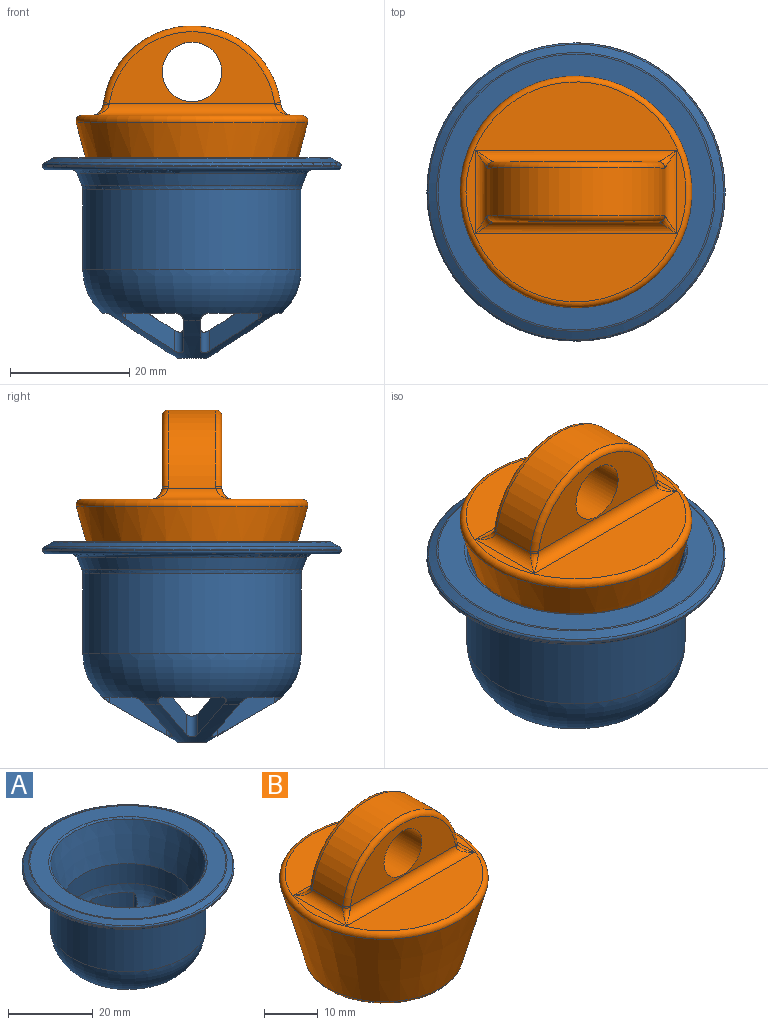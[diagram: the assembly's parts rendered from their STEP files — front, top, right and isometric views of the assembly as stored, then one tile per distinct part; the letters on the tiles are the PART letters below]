
ASSEMBLY  parts=2 mates=1
PART A: 55 faces, bbox 55.1x55.1x34.5 mm
  f0: torus R=8.3mm, axis (0,0,-1), area 945.5mm2, adj f1,f9,f14,f15,f16,f17,f18,f20
  f1: cone r=0mm half-angle=60deg, axis (0,0,1), area 270.6mm2, adj f0,f13,f14,f15,f19,f20,f21,f25
  f2: cone r=0mm half-angle=60deg, axis (0,0,1), area 183.2mm2, adj f3,f13,f14,f15,f19,f20,f21,f25
  f3: torus R=5.3mm, axis (0,0,-1), area 393.2mm2, adj f2,f10,f14,f15,f16,f17,f18,f20
  f4: cone r=25mm half-angle=60deg, axis (0,0,-1), area 238.5mm2, adj f50,f53
  f5: cylinder r=25mm len=50mm, axis (0,0,-1), area 33.2mm2, adj f50,f51
  f6: plane 49x49mm, normal (0,0,-1), area 606.8mm2, adj f7,f51
  f7: torus R=20.18mm, axis (0,0,-1), area 147mm2, adj f6,f8
  f8: cone r=18.3mm half-angle=21.8deg, axis (0,0,1), area 256.8mm2, adj f7,f54
  f9: cylinder r=18.3mm len=36.6mm, axis (0,0,-1), area 1526.5mm2, adj f0,f54
  f10: cylinder r=15.3mm len=30.6mm, axis (0,0,-1), area 551.1mm2, adj f3,f11
  f11: cone r=18.3mm half-angle=15deg, axis (0,0,1), area 1179.5mm2, adj f10,f52
  f12: plane 46.27x46.27mm, normal (0,0,1), area 584.7mm2, adj f52,f53
  f13: cylinder r=1mm len=3.46mm, axis (0,0,1), area 7.3mm2, adj f1,f2,f14,f15
  f14: plane 11.22x9.15mm, normal (-0.5,0.87,0), area 34.2mm2, adj f0,f1,f2,f3,f13,f18
  f15: plane 11.22x9.15mm, normal (-0.5,-0.87,0), area 34.2mm2, adj f0,f1,f2,f3,f13,f16
  f16: cylinder r=1mm len=7.62mm, axis (0,0,1), area 10.1mm2, adj f0,f3,f15,f17
  f17: cylinder r=15mm len=10.12mm, axis (0,0,1), area 69.4mm2, adj f0,f3,f16,f18
  f18: cylinder r=1mm len=7.62mm, axis (0,0,1), area 10.1mm2, adj f0,f3,f14,f17
  f19: cylinder r=1mm len=3.46mm, axis (0,0,1), area 7.3mm2, adj f1,f2,f20,f21
  f20: plane 11.22x9.15mm, normal (0.5,0.87,0), area 34.2mm2, adj f0,f1,f2,f3,f19,f24
  f21: plane 11.22x10.41mm, normal (-1,0,0), area 34.2mm2, adj f0,f1,f2,f3,f19,f22
  f22: cylinder r=1mm len=7.62mm, axis (0,0,1), area 10.1mm2, adj f0,f3,f21,f23
  f23: cylinder r=15mm len=8.76mm, axis (0,0,1), area 69.4mm2, adj f0,f3,f22,f24
  f24: cylinder r=1mm len=7.62mm, axis (0,0,1), area 10.1mm2, adj f0,f3,f20,f23
  f25: cylinder r=1mm len=3.46mm, axis (0,0,1), area 7.3mm2, adj f1,f2,f26,f27
  f26: plane 11.22x10.41mm, normal (-1,0,0), area 34.2mm2, adj f0,f1,f2,f3,f25,f30
  f27: plane 11.22x9.15mm, normal (0.5,-0.87,0), area 34.2mm2, adj f0,f1,f2,f3,f25,f28
  f28: cylinder r=1mm len=7.62mm, axis (0,0,1), area 10.1mm2, adj f0,f3,f27,f29
  f29: cylinder r=15mm len=8.76mm, axis (0,0,1), area 69.4mm2, adj f0,f3,f28,f30
  f30: cylinder r=1mm len=7.62mm, axis (0,0,1), area 10.1mm2, adj f0,f3,f26,f29
  f31: cylinder r=1mm len=3.46mm, axis (0,0,1), area 7.3mm2, adj f1,f2,f32,f33
  f32: plane 11.22x9.15mm, normal (-0.5,-0.87,0), area 34.2mm2, adj f0,f1,f2,f3,f31,f36
  f33: plane 11.22x10.41mm, normal (1,0,0), area 34.2mm2, adj f0,f1,f2,f3,f31,f34
  f34: cylinder r=1mm len=7.62mm, axis (0,0,1), area 10.1mm2, adj f0,f3,f33,f35
  f35: cylinder r=15mm len=8.76mm, axis (0,0,1), area 69.4mm2, adj f0,f3,f34,f36
  f36: cylinder r=1mm len=7.62mm, axis (0,0,1), area 10.1mm2, adj f0,f3,f32,f35
  f37: cylinder r=1mm len=3.46mm, axis (0,0,1), area 7.3mm2, adj f1,f2,f38,f39
  f38: plane 11.22x10.41mm, normal (1,0,0), area 34.2mm2, adj f0,f1,f2,f3,f37,f42
  f39: plane 11.22x9.15mm, normal (-0.5,0.87,0), area 34.2mm2, adj f0,f1,f2,f3,f37,f40
  f40: cylinder r=1mm len=7.62mm, axis (0,0,1), area 10.1mm2, adj f0,f3,f39,f41
  f41: cylinder r=15mm len=8.76mm, axis (0,0,1), area 69.4mm2, adj f0,f3,f40,f42
  f42: cylinder r=1mm len=7.62mm, axis (0,0,1), area 10.1mm2, adj f0,f3,f38,f41
  f43: cylinder r=1mm len=3.8mm, axis (0,0,1), area 7.3mm2, adj f1,f2,f44,f45
  f44: plane 11.22x9.15mm, normal (0.5,-0.87,0), area 34.2mm2, adj f0,f1,f2,f3,f43,f48
  f45: plane 11.22x9.15mm, normal (0.5,0.87,0), area 34.2mm2, adj f0,f1,f2,f3,f43,f46
  f46: cylinder r=1mm len=7.62mm, axis (0,0,1), area 10.1mm2, adj f0,f3,f45,f47
  f47: cylinder r=15mm len=10.12mm, axis (0,0,1), area 69.4mm2, adj f0,f3,f46,f48
  f48: cylinder r=1mm len=7.62mm, axis (0,0,1), area 10.1mm2, adj f0,f3,f44,f47
  f49: cylinder r=2.5mm len=5mm, axis (0,0,1), area 54.4mm2, adj f1,f2
  f50: torus R=24.5mm, axis (0,0,1), area 82mm2, adj f4,f5
  f51: torus R=24.5mm, axis (0,0,-1), area 122.5mm2, adj f5,f6
  f52: torus R=18.68mm, axis (0,0,1), area 75.7mm2, adj f11,f12
  f53: torus R=23.13mm, axis (0,0,1), area 38.3mm2, adj f4,f12
  f54: torus R=20.3mm, axis (0,0,-1), area 87.7mm2, adj f8,f9
PART B: 25 faces, bbox 42.1x42.1x35.8 mm
  f0: cone r=14.7mm half-angle=15deg, axis (0,0,1), area 1951.9mm2, adj f1,f6
  f1: torus R=13.73mm, axis (0,0,-1), area 117.6mm2, adj f0,f2
  f2: plane 27.47x27.47mm, normal (0,0,-1), area 203.6mm2, adj f1,f3
  f3: torus R=11.13mm, axis (0,0,-1), area 53.1mm2, adj f2,f4
  f4: cone r=10.42mm half-angle=45deg, axis (0,0,-1), area 482.3mm2, adj f3
  f5: plane 36.89x36.89mm, normal (0,0,1), area 596.3mm2, adj f6,f10,f11,f12,f13
  f6: torus R=18.45mm, axis (0,0,-1), area 220.3mm2, adj f0,f5
  f7: plane 27.71x12mm, normal (0,1,0), area 173.5mm2, adj f11,f21,f24
  f8: plane 27.71x12mm, normal (0,-1,0), area 173.5mm2, adj f12,f16,f24
  f9: cylinder r=15mm len=29.79mm, axis (0,-1,0), area 348.7mm2, adj f10,f13,f15,f16,f17,f20,f21,f22
  f10: cylinder r=2mm len=14mm, axis (0,-1,0), area 30.1mm2, adj f5,f9,f18,f19
  f11: cylinder r=2mm len=33.76mm, axis (-1,0,0), area 94.1mm2, adj f5,f7,f19,f20,f22,f23
  f12: cylinder r=2mm len=33.76mm, axis (1,0,0), area 94.1mm2, adj f5,f8,f14,f15,f17,f18
  f13: cylinder r=2mm len=14mm, axis (0,-1,0), area 30.1mm2, adj f5,f9,f14,f23
  f14: bspline ~3x3mm, area 3.3mm2, adj f12,f13,f15
  f15: bspline ~1.34x1.18mm, area 0.5mm2, adj f9,f12,f14,f16
  f16: torus R=14mm, axis (0,-1,0), area 65.6mm2, adj f8,f9,f15,f17
  f17: bspline ~1.9x1.23mm, area 0.5mm2, adj f9,f12,f16,f18
  f18: bspline ~3x3mm, area 3.3mm2, adj f10,f12,f17
  f19: bspline ~3x3mm, area 3.3mm2, adj f10,f11,f20
  f20: bspline ~1.34x1.18mm, area 0.5mm2, adj f9,f11,f19,f21
  f21: torus R=14mm, axis (0,-1,0), area 65.6mm2, adj f7,f9,f20,f22
  f22: bspline ~1.9x1.23mm, area 0.5mm2, adj f9,f11,f21,f23
  f23: bspline ~3x3mm, area 3.3mm2, adj f11,f13,f22
  f24: cylinder r=5mm len=10mm, axis (0,1,0), area 314.2mm2, adj f7,f8
PLACE A t=(-5.88,-3.57,-1.3)mm
PLACE B t=(-5.88,-3.57,21.24)mm
MATE cylindrical B.f0 <-> A.f0  axis (0,0,1) through (-5.88,-3.57,39.58)mm
